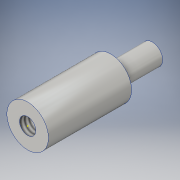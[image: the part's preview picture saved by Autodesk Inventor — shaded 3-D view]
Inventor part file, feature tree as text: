
AUTODESK INVENTOR PART (.ipt)
format: ipt  version: 2016 (Build 200138000, 138)  size: 115,200 bytes
history: native  units: in
note: dims shown in document units (in); Inventor stores cm internally (conversion verified against a paired STEP export)
features: sketch x4, extrude x2, hole x1
ambient origin geometry x8: Origin, YZ Plane, XZ Plane, XY Plane, X Axis, Y Axis, Z Axis, Center Point
bodies: Solid1 (feature_tree)
feature tree (7):
  extrude  "Extrusion1"  Depth=0.5in TaperAngle=0.0deg
  extrude  "Extrusion2"  Depth=1.0in TaperAngle=0.0deg
  sketch  "Sketch3"  dims[d13=0.196in d14=0.875in d15=0.375in d16=0.25in d17=0.5635in d18=0.875in d19=0.8108in]
  sketch  "Sketch4"
  hole  "Hole2"  [1 undecoded]
  sketch  "Sketch1"  dims[d0=0.25in d1=0.5in d2=0.0in]
  sketch  "Sketch2"  dims[d3=0.5in d4=1.0in d5=0.0in]
note: 1 required parameter value undecoded (feature->parameter linkage not recoverable at this tier; creation-order binding heuristic only, values carry confidence <= 0.55)
